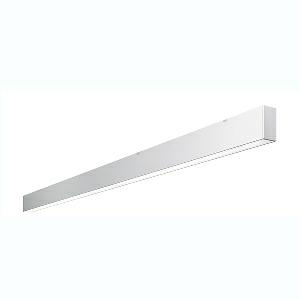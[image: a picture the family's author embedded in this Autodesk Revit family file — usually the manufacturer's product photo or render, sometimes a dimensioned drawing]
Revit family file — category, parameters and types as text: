
# Revit family: dotoo_line_-_dla_3000_840_d_end_00807936_6461
name_source: partatom
category: Lighting Fixtures
units: mm (PartAtom-declared; Revit-internal decimal feet)

## family parameters
Cut with Voids When Loaded = No
Host = Face
Light Source = No
Part Type = Normal
Room Calculation Point = No
Round Connector Dimension = Use Diameter
Shared = No

## types (1)
- DOTOO.line - DLA 3000/840/D END (1 x LED, 2750 lm, 4000K)
    Apparent Load = 26 VA
    Approval mark = CE
    CIE Flux Codes = 67 91 98 100 100
    Color Rendering = 80-89
    Color Temperature = 4000K
    Control Gear = Electronic ballast
    Default Elevation = 1800 mm
    Description = DLA 3000/840/D|Surface-mounted luminaire.|light source: LED|work equipment: Adjustable electronic ballast, digital DALI|connected load: 220-240 V, 50/60 Hz|Power consumption: approx. 26 W|luminous flux: 2750 lm|luminous efficacy: 105 lm/W|light distribution: Direct|colour temperature: Cold white, ca. 4000 K|class of protection: I|technology: Continuously dimmable|mains lead: Connector|glare control: Prism aperture|special features: DALI Load 1x, TouchDIM - dimming via standard switch, Through-wired, up to 18 m on one mains connection, Flicker-free, Suitable as emergency lighting, Mechanical and electrical connection of the individual modules without tools|
    Frequency = 50 Hz
    Height = 110 mm
    Lamp = 1 x LED
    Lamp Light Flux = 2750 lm
    Lamp count = 1
    Length = 2250 mm
    Luminous efficacy = 106 lm/W
    Manufacturer = Waldmann
    ModVariant = No
    Model = 00807936
    Mounting Place = Ceiling
    Mounting Type = Surface mounted
    Number of Poles = 1
    OnlyDefault = Yes
    Power Factor = 1
    Product Name = DOTOO.line - DLA 3000/840/D END
    Product group = Ceiling mounted luminaire
    ProductGroupID = 3
    Protection Class = Protection class I
    Protection Degree = IP 40
    RLX_Detail_Level = 1
    RLX_Emergency_Light_Flux = 0 lm
    RLX_Emergency_Type = 0
    RLX_Emergency_Type_DB = No
    RlxData = <blob elided: 19381 chars, md5=e85b6cd8>
    Socket = socket
    Standby Power = 0 W
    System Light Flux = 2750 lm
    System Power = 26 W
    Type Comments = Product without accessories
    Type Image = 114359000-00807936.jpg
    URL = http://relux.com
    VarID = ---
    Voltage = 230 V
    Voltage Range = 220-240 V
    Weight = 0.00 kg
    Width = 60 mm  [stored 0.19685 ft]

note: [stored X ft] marks values corroborated as IEEE doubles in the binary element streams (Revit-internal decimal feet)

## geometry (parser evidence)
native form markers: Blend x4, Sweep x10
no freeform markers — native parametric forms only
